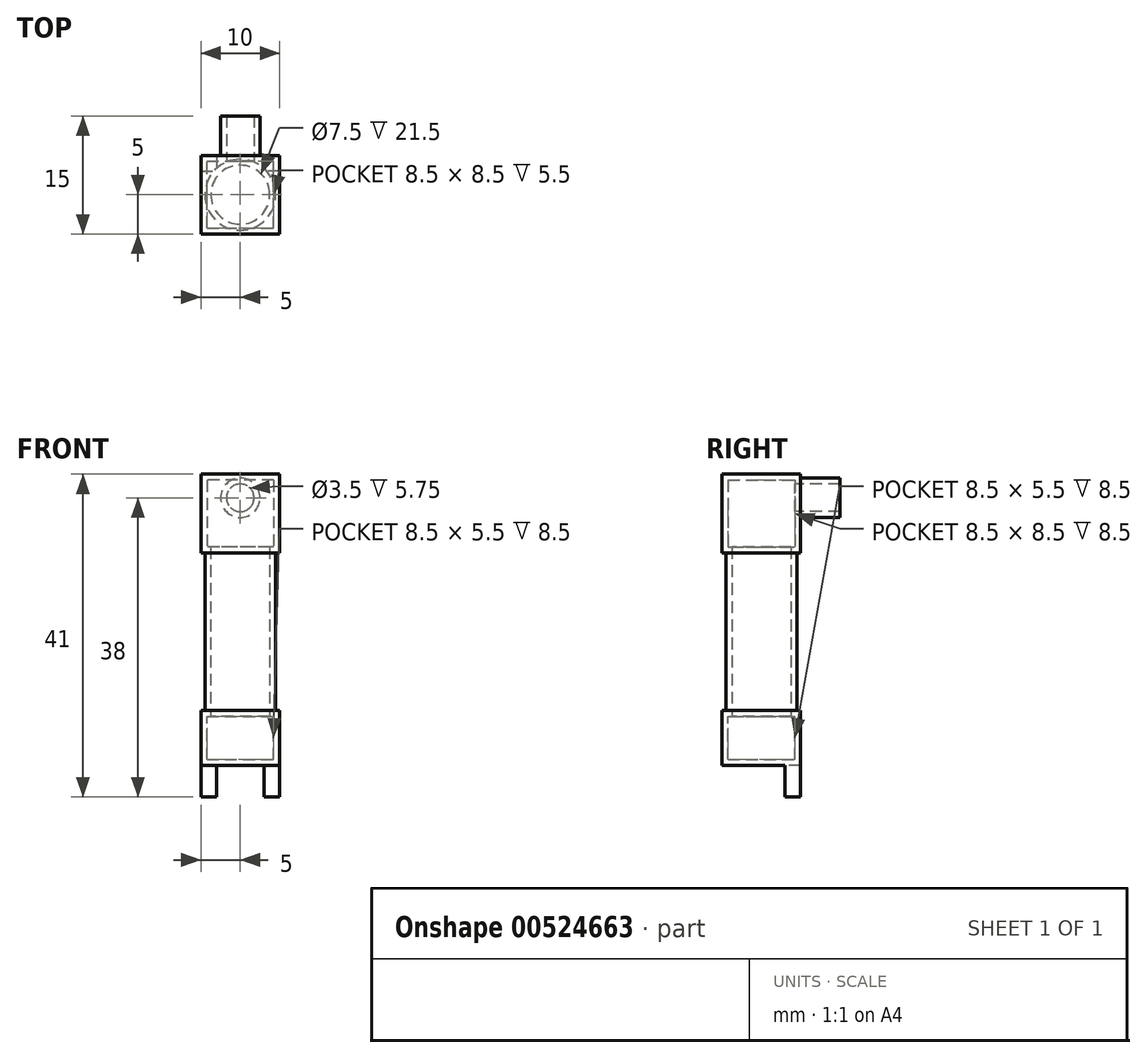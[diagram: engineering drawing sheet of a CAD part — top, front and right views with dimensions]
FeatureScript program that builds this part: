
annotation { "Feature Type Name" : "Feature", "Feature Type Description" : "" }
export const myFeature = defineFeature(function(context is Context, id is Id, definition is map)
    precondition{}
    {
        {
            var Q0;
            Q0=qCreatedBy(makeId("Top.planeOp"),FACE);
            var sketch = newSketch(context, id + "F0", { "sketchPlane" : qUnion([Q0])});
            skCircle(sketch, "E0", {"center": v(0, 0) * mm, "radius": 4.5 * mm});
            skLineSegment(sketch, "E1.bottom", {"start": v(-5, -5) * mm, "end": v(5, -5) * mm});
            skLineSegment(sketch, "E1.top", {"start": v(-5, 5) * mm, "end": v(5, 5) * mm});
            skLineSegment(sketch, "E1.left", {"start": v(-5, -5) * mm, "end": v(-5, 5) * mm});
            skLineSegment(sketch, "E1.right", {"start": v(5, -5) * mm, "end": v(5, 5) * mm});
            skSolve(sketch);
        }
        {
            var Q0;
            Q0=makeQuery(id+"F0.imprint","IMPRINT",FACE,{"disambiguationData":[TD([[makeQuery(id+"F0.imprint","IMPRINT",EDGE,{"derivedFrom":sQuery(id+"F0.wireOp",EDGE,"E0")}),1.0]])]});
            extrude(context, id + "F1", {"entities" : qUnion([Q0]), "depth" : 20 * mm, "offsetDistance" : 25 * mm});
        }
        {
            var Q0;
            Q0=makeQuery(id+"F0.imprint","IMPRINT",FACE,{"disambiguationData":[TD([[makeQuery(id+"F0.imprint","IMPRINT",EDGE,{"derivedFrom":sQuery(id+"F0.wireOp",EDGE,"E0")}),-1.0]])]});
            var Q1;
            Q1=makeQuery(id+"F0.imprint","IMPRINT",FACE,{"disambiguationData":[TD([[makeQuery(id+"F0.imprint","IMPRINT",EDGE,{"derivedFrom":sQuery(id+"F0.wireOp",EDGE,"E0")}),1.0]])]});
            extrude(context, id + "F2", {"entities" : qUnion([Q0, Q1]), "operationType" : NewBodyOperationType.ADD, "oppositeDirection" : true, "depth" : 7 * mm, "offsetDistance" : 25 * mm});
        }
        {
            var Q0;
            Q0=makeQuery(id+"F1.opExtrude","CAP_FACE",FACE,{"disambiguationData":[OSD([sQuery(id+"F0.wireOp",EDGE,"E0")])],"isStart":false});
            cPlane(context, id + "F3", {"entities" : qUnion([Q0]), "cplaneType" : CPlaneType.OFFSET, "offset" : 0 * mm, "width" : 150 * mm, "height" : 150 * mm});
        }
        {
            var Q0;
            Q0=qCreatedBy(id+"F3.planeOp",FACE);
            var sketch = newSketch(context, id + "F4", { "sketchPlane" : qUnion([Q0])});
            skLineSegment(sketch, "E2.bottom", {"start": v(5, -5) * mm, "end": v(-5, -5) * mm});
            skLineSegment(sketch, "E2.top", {"start": v(5, 5) * mm, "end": v(-5, 5) * mm});
            skLineSegment(sketch, "E2.left", {"start": v(5, -5) * mm, "end": v(5, 5) * mm});
            skLineSegment(sketch, "E2.right", {"start": v(-5, -5) * mm, "end": v(-5, 5) * mm});
            skPoint(sketch, "E2.middle", {"position": v(0, 0) * mm});
            skSolve(sketch);
        }
        {
            var Q0;
            Q0=makeQuery(id+"F4.imprint","IMPRINT",FACE,{"disambiguationData":[TD([[makeQuery(id+"F4.imprint","IMPRINT",EDGE,{"derivedFrom":sQuery(id+"F4.wireOp",EDGE,"E2.bottom")}),-1.0]])]});
            extrude(context, id + "F5", {"entities" : qUnion([Q0]), "operationType" : NewBodyOperationType.ADD, "depth" : 10 * mm, "offsetDistance" : 25 * mm});
        }
        {
            var Q0;
            Q0=makeQuery(id+"F5.opExtrude","SWEPT_FACE",FACE,{"disambiguationData":[OSD([sQuery(id+"F4.wireOp",EDGE,"E2.top")])]});
            var sketch = newSketch(context, id + "F6", { "sketchPlane" : qUnion([Q0])});
            skLineSegment(sketch, "E3", {"start": v(-5, 27) * mm, "end": v(0, 27) * mm, "construction": true});
            skLineSegment(sketch, "E4", {"start": v(0, 27) * mm, "end": v(0, 30) * mm, "construction": true});
            skCircle(sketch, "E5", {"center": v(0, 27) * mm, "radius": 2.5 * mm});
            skSolve(sketch);
        }
        {
            var Q0;
            Q0 = qSketchRegion(id + "F6", true);
            extrude(context, id + "F7", {"entities" : qUnion([Q0]), "operationType" : NewBodyOperationType.ADD, "depth" : 5 * mm, "offsetDistance" : 25 * mm});
        }
        {
            var Q0;
            Q0=makeQuery(id+"F7.opExtrude","CAP_FACE",FACE,{"disambiguationData":[OSD([sQuery(id+"F6.wireOp",EDGE,"E5")])],"isStart":false});
            shell(context, id + "F8", {"entities" : qUnion([Q0]), "thickness" : 0.75 * mm});
        }
        {
            var Q0;
            Q0=makeQuery(id+"F2.opExtrude","CAP_FACE",FACE,{"disambiguationData":[OSD([sQuery(id+"F0.wireOp",EDGE,"E1.bottom"),sQuery(id+"F0.wireOp",EDGE,"E1.top"),sQuery(id+"F0.wireOp",EDGE,"E1.left"),sQuery(id+"F0.wireOp",EDGE,"E1.right")])],"isStart":false});
            var sketch = newSketch(context, id + "F9", { "sketchPlane" : qUnion([Q0])});
            skLineSegment(sketch, "E6.bottom", {"start": v(5, -5) * mm, "end": v(3, -5) * mm});
            skLineSegment(sketch, "E6.top", {"start": v(5, -3) * mm, "end": v(3, -3) * mm});
            skLineSegment(sketch, "E6.left", {"start": v(5, -5) * mm, "end": v(5, -3) * mm});
            skLineSegment(sketch, "E6.right", {"start": v(3, -5) * mm, "end": v(3, -3) * mm});
            skLineSegment(sketch, "E7.bottom", {"start": v(-5, -5) * mm, "end": v(-3, -5) * mm});
            skLineSegment(sketch, "E7.top", {"start": v(-5, -3) * mm, "end": v(-3, -3) * mm});
            skLineSegment(sketch, "E7.left", {"start": v(-5, -5) * mm, "end": v(-5, -3) * mm});
            skLineSegment(sketch, "E7.right", {"start": v(-3, -5) * mm, "end": v(-3, -3) * mm});
            skSolve(sketch);
        }
        {
            var Q0;
            Q0 = qSketchRegion(id + "F9", true);
            extrude(context, id + "F10", {"entities" : qUnion([Q0]), "operationType" : NewBodyOperationType.ADD, "depth" : 4 * mm, "offsetDistance" : 25 * mm});
        }
    });
